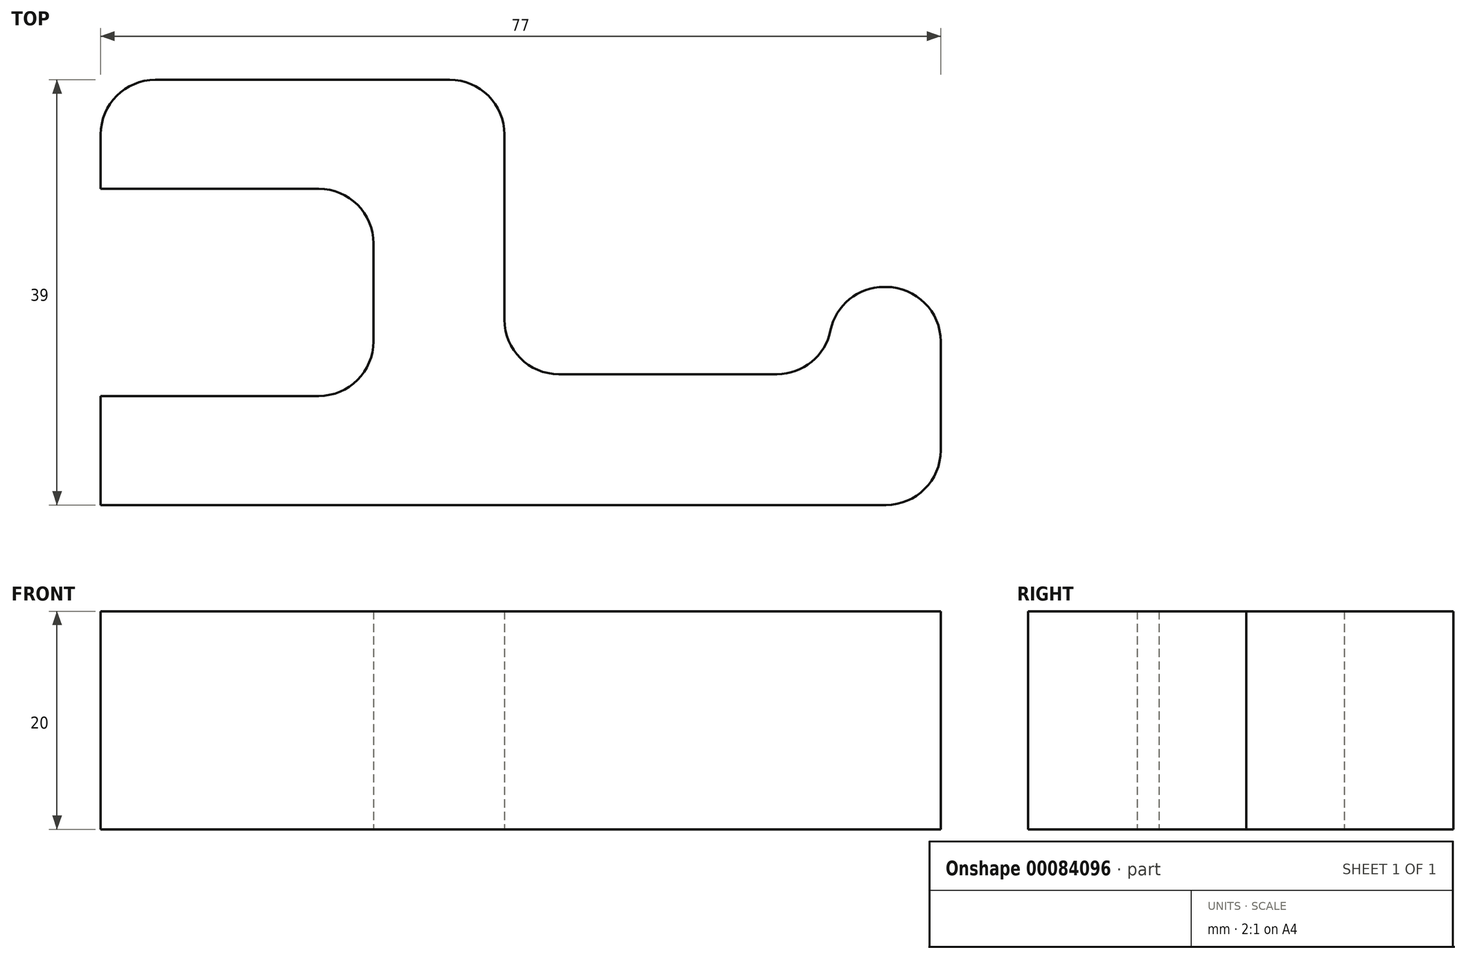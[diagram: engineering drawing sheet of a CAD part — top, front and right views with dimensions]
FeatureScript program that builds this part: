
annotation { "Feature Type Name" : "Feature", "Feature Type Description" : "" }
export const myFeature = defineFeature(function(context is Context, id is Id, definition is map)
    precondition{}
    {
        {
            var Q0;
            Q0=qCreatedBy(makeId("Front.planeOp"),FACE);
            var sketch = newSketch(context, id + "F0", { "sketchPlane" : qUnion([Q0])});
            skLineSegment(sketch, "E0", {"start": v(5, 39) * mm, "end": v(32, 39) * mm});
            skLineSegment(sketch, "E1", {"start": v(37, 34) * mm, "end": v(37, 17) * mm});
            skLineSegment(sketch, "E2", {"start": v(42, 12) * mm, "end": v(62, 12) * mm});
            skLineSegment(sketch, "E3", {"start": v(67, 17) * mm, "end": v(67, 20) * mm});
            skLineSegment(sketch, "E4", {"start": v(67, 20) * mm, "end": v(77, 20) * mm});
            skLineSegment(sketch, "E5", {"start": v(77, 20) * mm, "end": v(77, 5) * mm});
            skLineSegment(sketch, "E6", {"start": v(72, 0) * mm, "end": v(0, 0) * mm});
            skPoint(sketch, "E7.visualSharp", {"position": v(37, 12) * mm});
            skArc(sketch, "E7.filletArc", {"start": v(37, 17) * mm, "mid": v(38.46, 13.46) * mm, "end": v(42, 12) * mm});
            skPoint(sketch, "E8.visualSharp", {"position": v(67, 12) * mm});
            skArc(sketch, "E8.filletArc", {"start": v(62, 12) * mm, "mid": v(65.54, 13.46) * mm, "end": v(67, 17) * mm});
            skPoint(sketch, "E9.visualSharp", {"position": v(77, 0) * mm});
            skArc(sketch, "E9.filletArc", {"start": v(72, 0) * mm, "mid": v(75.54, 1.46) * mm, "end": v(77, 5) * mm});
            skLineSegment(sketch, "E10", {"start": v(0, 29) * mm, "end": v(20, 29) * mm});
            skLineSegment(sketch, "E11", {"start": v(25, 24) * mm, "end": v(25, 15) * mm});
            skLineSegment(sketch, "E12", {"start": v(20, 10) * mm, "end": v(0, 10) * mm});
            skLineSegment(sketch, "E13", {"start": v(0, 10) * mm, "end": v(0, 0) * mm});
            skPoint(sketch, "E14.visualSharp", {"position": v(25, 10) * mm});
            skArc(sketch, "E14.filletArc", {"start": v(20, 10) * mm, "mid": v(23.54, 11.46) * mm, "end": v(25, 15) * mm});
            skArc(sketch, "E15.filletArc", {"start": v(25, 24) * mm, "mid": v(23.54, 27.54) * mm, "end": v(20, 29) * mm});
            skPoint(sketch, "E16.visualSharp", {"position": v(37, 39) * mm});
            skArc(sketch, "E16.filletArc", {"start": v(37, 34) * mm, "mid": v(35.54, 37.54) * mm, "end": v(32, 39) * mm});
            skPoint(sketch, "E17.visualSharp", {"position": v(0, 29) * mm});
            skPoint(sketch, "E18.visualSharp", {"position": v(0, 39) * mm});
            skArc(sketch, "E18.filletArc", {"start": v(5, 39) * mm, "mid": v(1.46, 37.54) * mm, "end": v(0, 34) * mm});
            skLineSegment(sketch, "E19", {"start": v(0, 34) * mm, "end": v(0, 29) * mm});
            skSolve(sketch);
        }
        {
            var Q0;
            Q0 = qSketchRegion(id + "F0", true);
            extrude(context, id + "F1", {"entities" : qUnion([Q0]), "depth" : 20 * mm, "offsetDistance" : 25 * mm});
        }
        {
            var Q0;
            Q0=makeQuery(id+"F1.opExtrude","SWEPT_EDGE",EDGE,{"disambiguationData":[OSD([sQuery(id+"F0.wireOp",EDGE,"E3"),sQuery(id+"F0.wireOp",EDGE,"E4")])]});
            fillet(context, id + "F2", {"entities" : qUnion([Q0]), "radius" : 5 * mm, "tangentPropagation" : true, "allowEdgeOverflow" : false});
        }
        {
            var Q0;
            Q0=makeQuery(id+"F1.opExtrude","SWEPT_EDGE",EDGE,{"disambiguationData":[OSD([sQuery(id+"F0.wireOp",EDGE,"E4"),sQuery(id+"F0.wireOp",EDGE,"E5")])]});
            fillet(context, id + "F3", {"entities" : qUnion([Q0]), "radius" : 5 * mm, "tangentPropagation" : true, "allowEdgeOverflow" : false});
        }
        {
            var Q0;
            Q0=makeQuery(id+"F1.opExtrude","SWEPT_BODY",BODY,{"disambiguationData":[OSD([sQuery(id+"F0.wireOp",EDGE,"E0"),sQuery(id+"F0.wireOp",EDGE,"E1"),sQuery(id+"F0.wireOp",EDGE,"E2"),sQuery(id+"F0.wireOp",EDGE,"E3"),sQuery(id+"F0.wireOp",EDGE,"E4"),sQuery(id+"F0.wireOp",EDGE,"E5"),sQuery(id+"F0.wireOp",EDGE,"E6"),sQuery(id+"F0.wireOp",EDGE,"E7.filletArc"),sQuery(id+"F0.wireOp",EDGE,"E8.filletArc"),sQuery(id+"F0.wireOp",EDGE,"E9.filletArc"),sQuery(id+"F0.wireOp",EDGE,"E10"),sQuery(id+"F0.wireOp",EDGE,"E11"),sQuery(id+"F0.wireOp",EDGE,"E12"),sQuery(id+"F0.wireOp",EDGE,"E13"),sQuery(id+"F0.wireOp",EDGE,"E14.filletArc"),sQuery(id+"F0.wireOp",EDGE,"E15.filletArc"),sQuery(id+"F0.wireOp",EDGE,"E16.filletArc"),sQuery(id+"F0.wireOp",EDGE,"E18.filletArc"),sQuery(id+"F0.wireOp",EDGE,"E19")])]});
            var Q1;
            Q1=makeQuery(id+"F1.opExtrude","CAP_EDGE",EDGE,{"disambiguationData":[OSD([sQuery(id+"F0.wireOp",EDGE,"E6")])],"isStart":true});
            var Q2;
            Q2=makeQuery(id+"F1.opExtrude","CAP_EDGE",EDGE,{"disambiguationData":[OSD([sQuery(id+"F0.wireOp",EDGE,"E6")])],"isStart":true});
            transform(context, id + "F4", {"entities" : qUnion([Q0]), "transformType" : TransformType.ROTATION, "transformAxis" : qUnion([Q2]), "angle" : 90 * degree, "makeCopy" : false});
        }
    });
